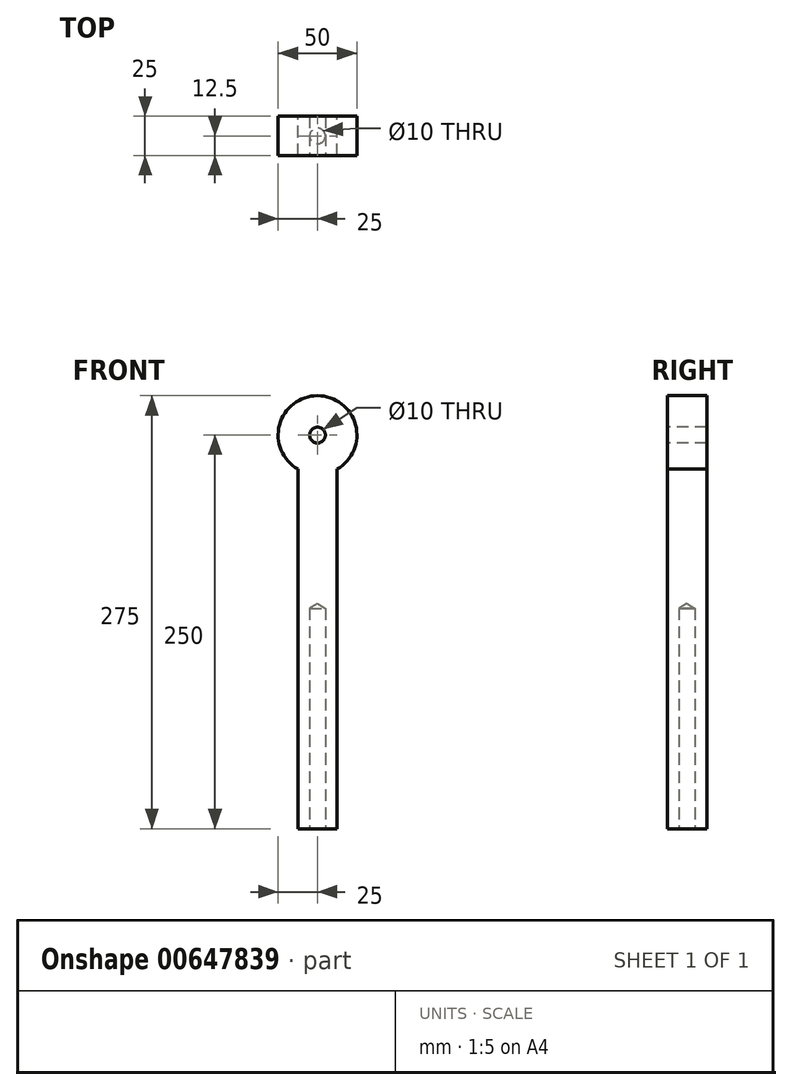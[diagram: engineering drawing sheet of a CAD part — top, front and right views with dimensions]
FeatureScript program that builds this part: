
annotation { "Feature Type Name" : "Feature", "Feature Type Description" : "" }
export const myFeature = defineFeature(function(context is Context, id is Id, definition is map)
    precondition{}
    {
        {
            var Q0;
            Q0=qCreatedBy(makeId("Front.planeOp"),FACE);
            var sketch = newSketch(context, id + "F0", { "sketchPlane" : qUnion([Q0])});
            skLineSegment(sketch, "E0.bottom", {"start": v(-12.5, -125) * mm, "end": v(12.5, -125) * mm});
            skLineSegment(sketch, "E0.top", {"start": v(-12.5, 125) * mm, "end": v(12.5, 125) * mm});
            skLineSegment(sketch, "E0.left", {"start": v(-12.5, -125) * mm, "end": v(-12.5, 125) * mm});
            skLineSegment(sketch, "E0.right", {"start": v(12.5, -125) * mm, "end": v(12.5, 125) * mm});
            skPoint(sketch, "E0.middle", {"position": v(0, 0) * mm});
            skPoint(sketch, "E1", {"position": v(0, 125) * mm});
            skCircle(sketch, "E2", {"center": v(0, 125) * mm, "radius": 25 * mm});
            skSolve(sketch);
        }
        {
            var Q0;
            {var subQ0=sQuery(id+"F0.wireOp",EDGE,"E0.bottom");Q0=makeQuery(id+"F0.imprint","IMPRINT",FACE,{"disambiguationData":[TD([[makeQuery(id+"F0.imprint","IMPRINT",EDGE,{"derivedFrom":subQ0}),1.0]])]});}
            extrude(context, id + "F1", {"entities" : qUnion([Q0]), "depth" : 25 * mm, "offsetDistance" : 25 * mm});
        }
        {
            var Q0;
            Q0 = qSketchRegion(id + "F0", true);
            extrude(context, id + "F2", {"entities" : qUnion([Q0]), "operationType" : NewBodyOperationType.ADD, "depth" : 25 * mm, "offsetDistance" : 25 * mm});
        }
        {
            var Q0;
            Q0=makeQuery(id+"F1.opExtrude","SWEPT_FACE",FACE,{"disambiguationData":[OSD([sQuery(id+"F0.wireOp",EDGE,"E0.bottom")])]});
            var sketch = newSketch(context, id + "F3", { "sketchPlane" : qUnion([Q0])});
            skPoint(sketch, "E3", {"position": v(0, 12.5) * mm});
            skSolve(sketch);
        }
        {
            var Q0;
            Q0=sQuery(id+"F3.wireOp",VERTEX,"E3");
            var Q1;
            Q1=makeQuery(id+"F1.opExtrude","SWEPT_BODY",BODY,{"disambiguationData":[OSD([sQuery(id+"F0.wireOp",EDGE,"E0.bottom"),sQuery(id+"F0.wireOp",EDGE,"E0.left"),sQuery(id+"F0.wireOp",EDGE,"E0.right"),sQuery(id+"F0.wireOp",EDGE,"E2")])]});
            hole(context, id + "F4", {"style" : HoleStyle.SIMPLE, "endStyle" : HoleEndStyle.BLIND, "holeDiameter" : 10 * mm, "majorDiameter" : 5 * mm, "holeDepth" : 140 * mm, "isTappedThrough" : true, "tappedDepth" : 12 * mm, "tapClearance" : 3, "locations" : qUnion([Q0]), "scope" : qUnion([Q1])});
        }
        {
            var Q0;
            {var subQ0=sQuery(id+"F0.wireOp",EDGE,"E2");var subQ1=sQuery(id+"F0.wireOp",EDGE,"E0.right");var subQ2=sQuery(id+"F0.wireOp",EDGE,"E0.left");var subQ3=sQuery(id+"F0.wireOp",EDGE,"E0.bottom");Q0=makeQuery(id+"F2.boolean.opBoolean","MERGE",FACE,{"derivedFrom":[makeQuery(id+"F1.opExtrude","CAP_FACE",FACE,{"disambiguationData":[OSD([subQ3,subQ2,subQ1,subQ0])],"isStart":false}),makeQuery(id+"F2.opExtrude","CAP_FACE",FACE,{"disambiguationData":[OSD([subQ3,subQ2,subQ1,subQ0])],"isStart":false})]});}
            var sketch = newSketch(context, id + "F5", { "sketchPlane" : qUnion([Q0])});
            skPoint(sketch, "E4", {"position": v(0, 125) * mm});
            skSolve(sketch);
        }
        {
            var Q0;
            Q0=sQuery(id+"F5.wireOp",VERTEX,"E4");
            var Q1;
            Q1=makeQuery(id+"F1.opExtrude","SWEPT_BODY",BODY,{"disambiguationData":[OSD([sQuery(id+"F0.wireOp",EDGE,"E0.bottom"),sQuery(id+"F0.wireOp",EDGE,"E0.left"),sQuery(id+"F0.wireOp",EDGE,"E0.right"),sQuery(id+"F0.wireOp",EDGE,"E2")])]});
            hole(context, id + "F6", {"style" : HoleStyle.SIMPLE, "endStyle" : HoleEndStyle.THROUGH, "holeDiameter" : 10 * mm, "majorDiameter" : 5 * mm, "isTappedThrough" : true, "tappedDepth" : 12 * mm, "tapClearance" : 3, "locations" : qUnion([Q0]), "scope" : qUnion([Q1])});
        }
    });
